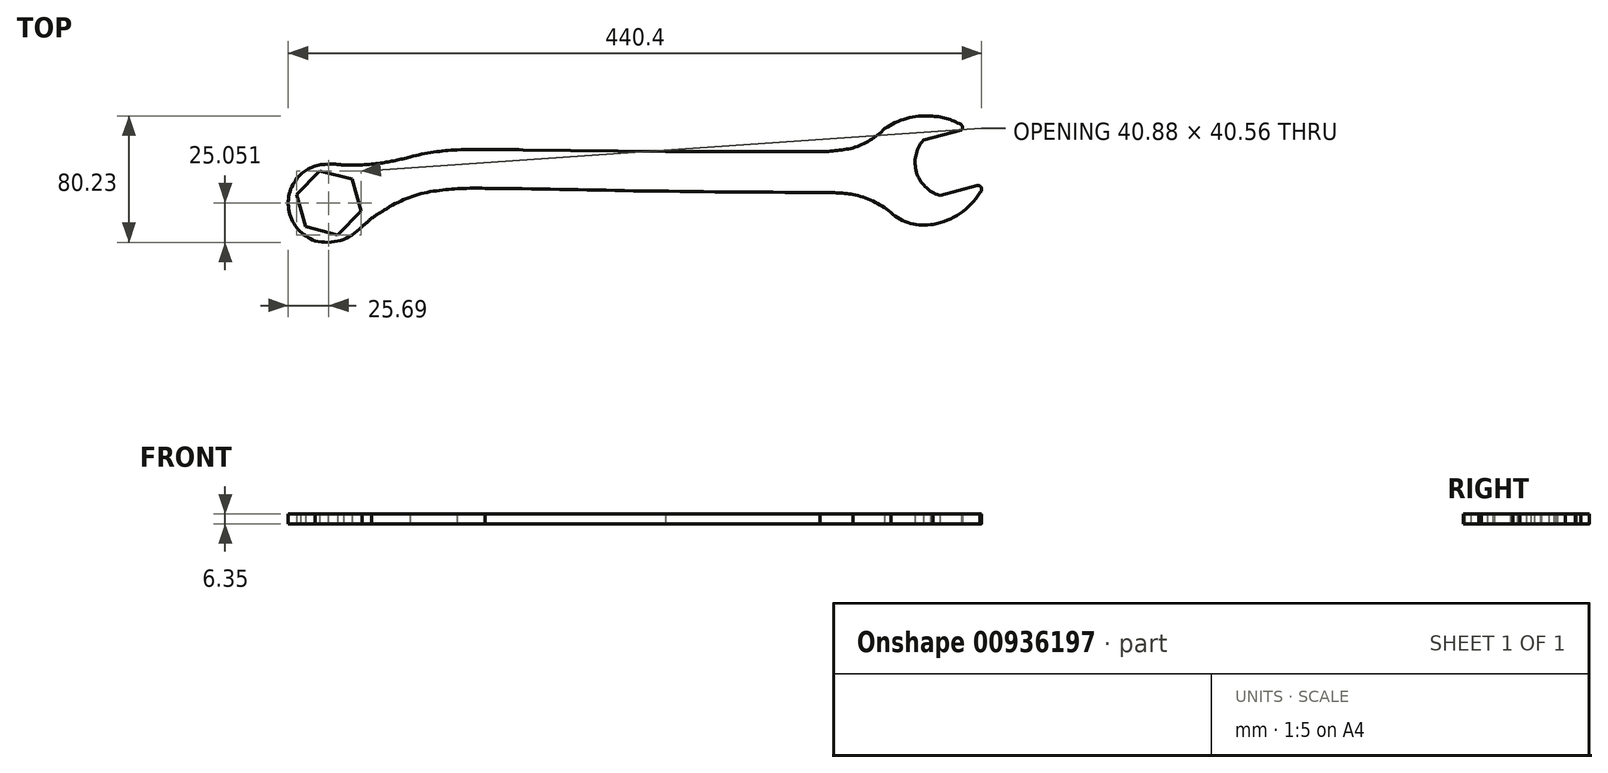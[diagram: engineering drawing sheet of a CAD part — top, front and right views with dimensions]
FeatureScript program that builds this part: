
annotation { "Feature Type Name" : "Feature", "Feature Type Description" : "" }
export const myFeature = defineFeature(function(context is Context, id is Id, definition is map)
    precondition{}
    {
        {
            var Q0;
            Q0=qCreatedBy(makeId("Top.planeOp"),FACE);
            var sketch = newSketch(context, id + "F0", { "sketchPlane" : qUnion([Q0])});
            skLineSegment(sketch, "E0", {"start": v(-52.55, 160.32) * mm, "end": v(-76.66, 153.95) * mm});
            skLineSegment(sketch, "E1", {"start": v(-42.67, 125.16) * mm, "end": v(-66.15, 118.95) * mm});
            skLineSegment(sketch, "E2", {"start": v(-144.08, 146.66) * mm, "end": v(-240.2, 146.66) * mm});
            skLineSegment(sketch, "E3", {"start": v(-240.2, 146.66) * mm, "end": v(-330.83, 147.86) * mm});
            skArc(sketch, "E4", {"start": v(-330.83, 147.86) * mm, "mid": v(-351.76, 148.02) * mm, "end": v(-372.69, 147.86) * mm});
            skArc(sketch, "E5", {"start": v(-372.69, 147.86) * mm, "mid": v(-387.74, 146.37) * mm, "end": v(-402.57, 143.4) * mm});
            skArc(sketch, "E6", {"start": v(-421.3, 139.4) * mm, "mid": v(-411.87, 141.07) * mm, "end": v(-402.57, 143.4) * mm});
            skArc(sketch, "E7", {"start": v(-444.95, 138.11) * mm, "mid": v(-433.1, 138.26) * mm, "end": v(-421.3, 139.4) * mm});
            skArc(sketch, "E8", {"start": v(-444.95, 138.11) * mm, "mid": v(-449.7, 138.7) * mm, "end": v(-454.5, 138.67) * mm});
            skArc(sketch, "E9", {"start": v(-415.44, 111.71) * mm, "mid": v(-421.24, 108.16) * mm, "end": v(-426.95, 104.46) * mm});
            skArc(sketch, "E10", {"start": v(-385.9, 121.84) * mm, "mid": v(-401.16, 118.23) * mm, "end": v(-415.44, 111.71) * mm});
            skArc(sketch, "E11", {"start": v(-354.93, 123.4) * mm, "mid": v(-370.44, 123.26) * mm, "end": v(-385.9, 121.84) * mm});
            skArc(sketch, "E12", {"start": v(-260.57, 121.84) * mm, "mid": v(-307.75, 122.78) * mm, "end": v(-354.93, 123.4) * mm});
            skArc(sketch, "E13", {"start": v(-260.57, 121.84) * mm, "mid": v(-201.47, 121.12) * mm, "end": v(-142.37, 120.76) * mm});
            skArc(sketch, "E14", {"start": v(-121.27, 119.61) * mm, "mid": v(-131.8, 120.55) * mm, "end": v(-142.37, 120.76) * mm});
            skArc(sketch, "E15", {"start": v(-97.31, 108.1) * mm, "mid": v(-108.6, 115.27) * mm, "end": v(-121.27, 119.61) * mm});
            skArc(sketch, "E16", {"start": v(-97.31, 108.1) * mm, "mid": v(-84.73, 101.16) * mm, "end": v(-70.37, 100.57) * mm});
            skArc(sketch, "E17", {"start": v(-70.37, 100.57) * mm, "mid": v(-53.28, 107.45) * mm, "end": v(-40.53, 120.76) * mm});
            skArc(sketch, "E18", {"start": v(-40.53, 120.76) * mm, "mid": v(-39.79, 123.84) * mm, "end": v(-42.67, 125.16) * mm});
            skArc(sketch, "E19", {"start": v(-144.08, 146.66) * mm, "mid": v(-132.61, 147.25) * mm, "end": v(-121.27, 148.99) * mm});
            skArc(sketch, "E20", {"start": v(-121.27, 148.99) * mm, "mid": v(-110.52, 154) * mm, "end": v(-101.14, 161.28) * mm});
            skArc(sketch, "E21", {"start": v(-72.1, 169.2) * mm, "mid": v(-87.3, 167.78) * mm, "end": v(-101.14, 161.28) * mm});
            skArc(sketch, "E22", {"start": v(-52.54, 163.77) * mm, "mid": v(-61.96, 167.79) * mm, "end": v(-72.1, 169.2) * mm});
            skArc(sketch, "E23", {"start": v(-52.55, 160.32) * mm, "mid": v(-51.7, 162.04) * mm, "end": v(-52.54, 163.77) * mm});
            skArc(sketch, "E24", {"start": v(-76.66, 153.95) * mm, "mid": v(-80.94, 133.6) * mm, "end": v(-66.15, 118.95) * mm});
            skCircle(sketch, "E25.cCircle", {"center": v(-454.25, 114.16) * mm, "radius": 18.26 * mm, "construction": true});
            skLineSegment(sketch, "E25.0", {"start": v(-468.94, 99.04) * mm, "end": v(-474.69, 119.33) * mm});
            skLineSegment(sketch, "E25.1", {"start": v(-474.69, 119.33) * mm, "end": v(-460, 134.44) * mm});
            skLineSegment(sketch, "E25.2", {"start": v(-460, 134.44) * mm, "end": v(-439.56, 129.28) * mm});
            skLineSegment(sketch, "E25.3", {"start": v(-439.56, 129.28) * mm, "end": v(-433.81, 109) * mm});
            skLineSegment(sketch, "E25.4", {"start": v(-433.81, 109) * mm, "end": v(-448.5, 93.88) * mm});
            skLineSegment(sketch, "E25.5", {"start": v(-448.5, 93.88) * mm, "end": v(-468.94, 99.04) * mm});
            skPoint(sketch, "E25.0.midPoint", {"position": v(-471.82, 109.18) * mm});
            skArc(sketch, "E26", {"start": v(-462.97, 90.09) * mm, "mid": v(-446.78, 90.37) * mm, "end": v(-433.1, 99.03) * mm});
            skArc(sketch, "E27", {"start": v(-472.2, 132.2) * mm, "mid": v(-479.35, 108.57) * mm, "end": v(-462.97, 90.09) * mm});
            skPoint(sketch, "E27.startSnap0", {"position": v(-472.2, 96.53) * mm});
            skArc(sketch, "E28", {"start": v(-454.5, 138.67) * mm, "mid": v(-463.99, 137.2) * mm, "end": v(-472.2, 132.2) * mm});
            skArc(sketch, "E29", {"start": v(-426.95, 104.46) * mm, "mid": v(-430.05, 101.77) * mm, "end": v(-433.1, 99.03) * mm});
            skSolve(sketch);
        }
        {
            var Q0;
            Q0=makeQuery(id+"F0.imprint","IMPRINT",FACE,{"disambiguationData":[TD([[makeQuery(id+"F0.imprint","IMPRINT",EDGE,{"derivedFrom":sQuery(id+"F0.wireOp",EDGE,"E0")}),-1.0]])]});
            extrude(context, id + "F1", {"entities" : qUnion([Q0]), "depth" : 6.35 * mm, "offsetDistance" : 25.4 * mm});
        }
    });
